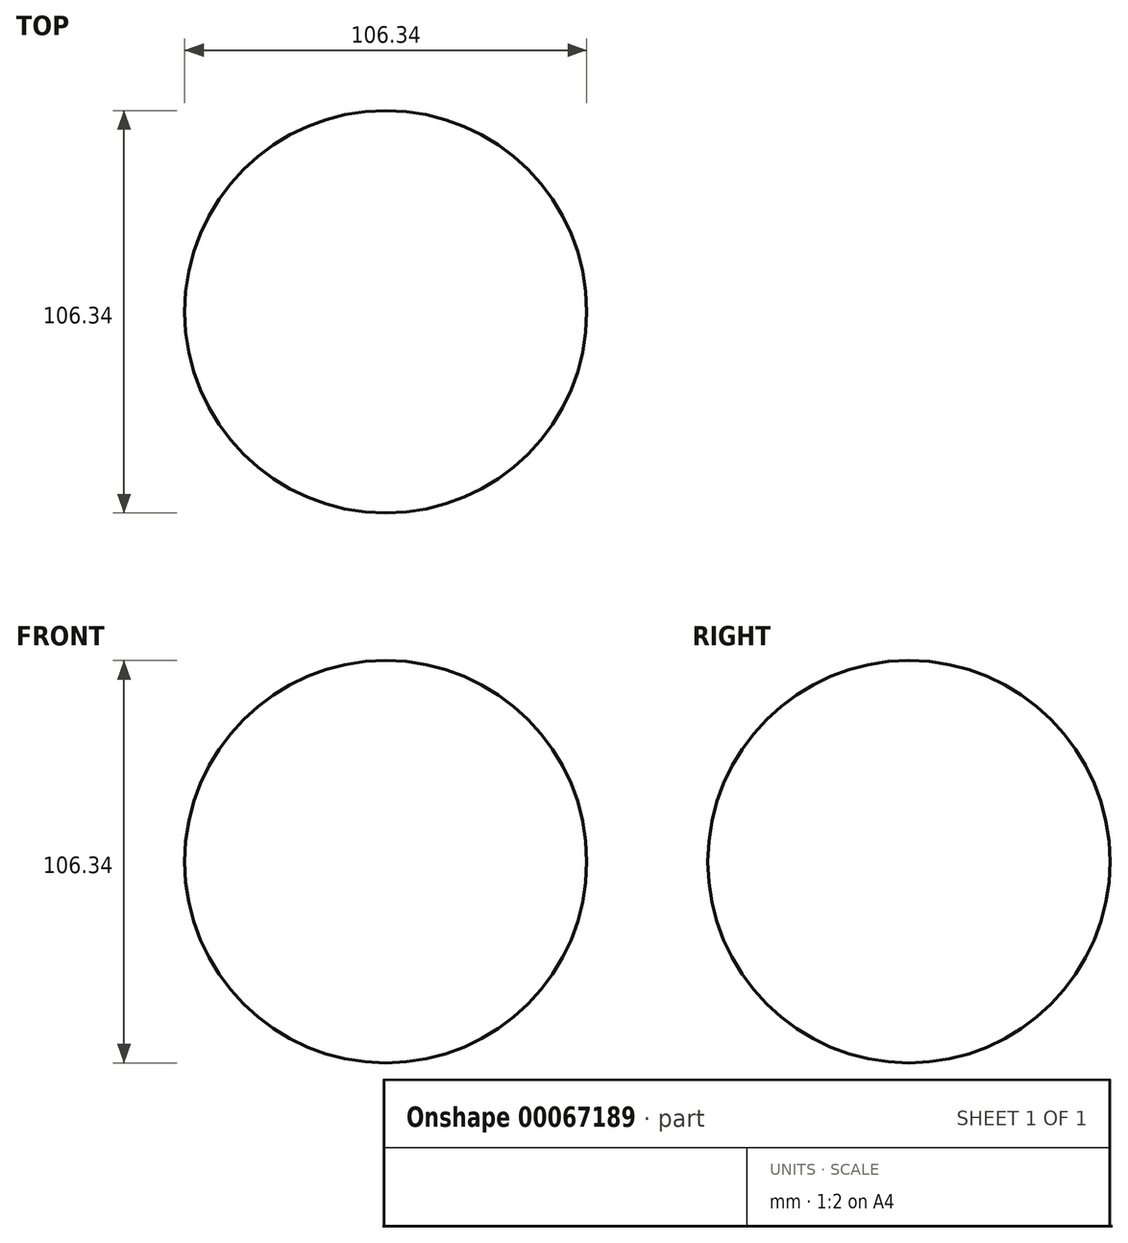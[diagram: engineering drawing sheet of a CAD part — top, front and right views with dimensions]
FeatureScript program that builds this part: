
annotation { "Feature Type Name" : "Feature", "Feature Type Description" : "" }
export const myFeature = defineFeature(function(context is Context, id is Id, definition is map)
    precondition{}
    {
        {
            var Q0;
            Q0=qCreatedBy(makeId("Front.planeOp"),FACE);
            var sketch = newSketch(context, id + "F0", { "sketchPlane" : qUnion([Q0])});
            skCircle(sketch, "E0", {"center": v(0, 0) * mm, "radius": 53.17 * mm});
            skLineSegment(sketch, "E1", {"start": v(0, 0) * mm, "end": v(0, -53.17) * mm});
            skLineSegment(sketch, "E2", {"start": v(0, -53.17) * mm, "end": v(0, 53.17) * mm});
            skSolve(sketch);
        }
        {
            var Q0;
            {var subQ0=sQuery(id+"F0.wireOp",EDGE,"E2");var subQ4=makeQuery(id+"F0.imprint","IMPRINT",VERTEX,{"derivedFrom":subQ0});Q0=makeQuery(id+"F0.imprint","IMPRINT",FACE,{"disambiguationData":[TD([[makeQuery(id+"F0.imprint","IMPRINT",EDGE,{"disambiguationData":[TD([[subQ4,1.0]])],"derivedFrom":subQ0}),-1.0]])]});}
            var Q1;
            Q1=sQuery(id+"F0.wireOp",EDGE,"E2");
            revolve(context, id + "F1", {"entities" : qUnion([Q0]), "axis" : qUnion([Q1]), "revolveType" : RevolveType.FULL});
        }
    });
